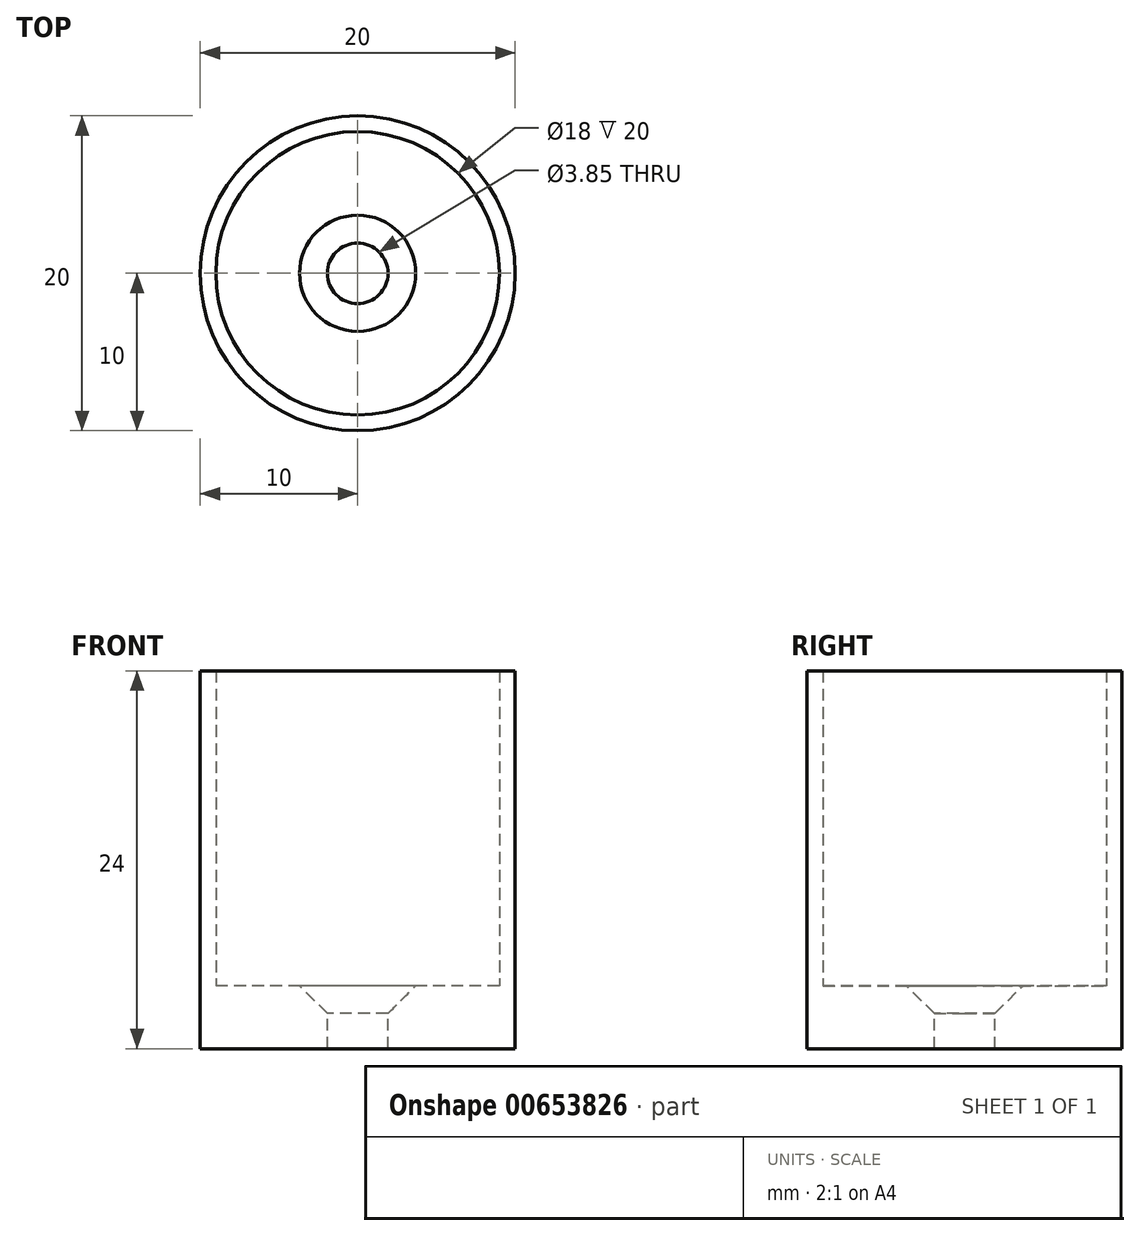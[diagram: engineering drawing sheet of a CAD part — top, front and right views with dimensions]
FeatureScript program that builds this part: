
annotation { "Feature Type Name" : "Feature", "Feature Type Description" : "" }
export const myFeature = defineFeature(function(context is Context, id is Id, definition is map)
    precondition{}
    {
        {
            var Q0;
            Q0=qCreatedBy(makeId("Top.planeOp"),FACE);
            var sketch = newSketch(context, id + "F0", { "sketchPlane" : qUnion([Q0])});
            skCircle(sketch, "E0", {"center": v(0, 0) * mm, "radius": 10 * mm});
            skCircle(sketch, "E1", {"center": v(0, 0) * mm, "radius": 9 * mm});
            skLineSegment(sketch, "E2", {"start": v(-9.77, 2.12) * mm, "end": v(9.77, 2.12) * mm});
            skSolve(sketch);
        }
        {
            var Q0;
            {var subQ0=sQuery(id+"F0.wireOp",EDGE,"E2");var subQ1=sQuery(id+"F0.wireOp",EDGE,"E0");var subQ2=makeQuery(id+"F0.imprint","INTERSECT",VERTEX,{"disambiguationData":[OD(0.0)],"derivedFrom":[subQ1,subQ0]});Q0=makeQuery(id+"F0.imprint","IMPRINT",FACE,{"disambiguationData":[TD([[makeQuery(id+"F0.imprint","IMPRINT",EDGE,{"disambiguationData":[TD([[subQ2,-1.0]])],"derivedFrom":subQ1}),1.0]])]});}
            extrude(context, id + "F1", {"entities" : qUnion([Q0]), "depth" : 20 * mm, "offsetDistance" : 25 * mm});
        }
        {
            var Q0;
            {var subQ0=sQuery(id+"F0.wireOp",EDGE,"E2");var subQ1=sQuery(id+"F0.wireOp",EDGE,"E1");var subQ2=makeQuery(id+"F0.imprint","INTERSECT",VERTEX,{"disambiguationData":[OD(0.0)],"derivedFrom":[subQ1,subQ0]});Q0=makeQuery(id+"F0.imprint","IMPRINT",FACE,{"disambiguationData":[TD([[makeQuery(id+"F0.imprint","IMPRINT",EDGE,{"disambiguationData":[TD([[subQ2,1.0]])],"derivedFrom":subQ1}),1.0]])]});}
            var Q1;
            {var subQ0=sQuery(id+"F0.wireOp",EDGE,"E2");var subQ1=sQuery(id+"F0.wireOp",EDGE,"E0");var subQ2=makeQuery(id+"F0.imprint","INTERSECT",VERTEX,{"disambiguationData":[OD(0.0)],"derivedFrom":[subQ1,subQ0]});Q1=makeQuery(id+"F0.imprint","IMPRINT",FACE,{"disambiguationData":[TD([[makeQuery(id+"F0.imprint","IMPRINT",EDGE,{"disambiguationData":[TD([[subQ2,1.0]])],"derivedFrom":subQ1}),1.0]])]});}
            var Q2;
            {var subQ0=sQuery(id+"F0.wireOp",EDGE,"E2");var subQ1=sQuery(id+"F0.wireOp",EDGE,"E0");var subQ2=makeQuery(id+"F0.imprint","INTERSECT",VERTEX,{"disambiguationData":[OD(0.0)],"derivedFrom":[subQ1,subQ0]});Q2=makeQuery(id+"F0.imprint","IMPRINT",FACE,{"disambiguationData":[TD([[makeQuery(id+"F0.imprint","IMPRINT",EDGE,{"disambiguationData":[TD([[subQ2,-1.0]])],"derivedFrom":subQ1}),1.0]])]});}
            var Q3;
            {var subQ0=sQuery(id+"F0.wireOp",EDGE,"E2");var subQ1=sQuery(id+"F0.wireOp",EDGE,"E1");var subQ2=makeQuery(id+"F0.imprint","INTERSECT",VERTEX,{"disambiguationData":[OD(0.0)],"derivedFrom":[subQ1,subQ0]});Q3=makeQuery(id+"F0.imprint","IMPRINT",FACE,{"disambiguationData":[TD([[makeQuery(id+"F0.imprint","IMPRINT",EDGE,{"disambiguationData":[TD([[subQ2,-1.0]])],"derivedFrom":subQ1}),1.0]])]});}
            extrude(context, id + "F2", {"entities" : qUnion([Q0, Q1, Q2, Q3]), "operationType" : NewBodyOperationType.ADD, "oppositeDirection" : true, "depth" : 4 * mm, "offsetDistance" : 25 * mm});
        }
        {
            var Q0;
            Q0=makeQuery(id+"F2.opExtrude","CAP_FACE",FACE,{"disambiguationData":[OSD([sQuery(id+"F0.wireOp",EDGE,"E0")])],"isStart":true});
            var sketch = newSketch(context, id + "F3", { "sketchPlane" : qUnion([Q0])});
            skCircle(sketch, "E3", {"center": v(0, 0) * mm, "radius": 1.38 * mm});
            skSolve(sketch);
        }
        {
            var Q0;
            Q0=sQuery(id+"F3.wireOp",VERTEX,"E3.center");
            var Q1;
            Q1=makeQuery(id+"F1.opExtrude","SWEPT_BODY",BODY,{"disambiguationData":[OSD([sQuery(id+"F0.wireOp",EDGE,"E0"),sQuery(id+"F0.wireOp",EDGE,"E1"),sQuery(id+"F0.wireOp",EDGE,"E2")])]});
            hole(context, id + "F4", {"style" : HoleStyle.C_SINK, "endStyle" : HoleEndStyle.THROUGH, "holeDiameter" : 3.85 * mm, "cSinkDiameter" : 7.38 * mm, "cSinkAngle" : 90 * degree, "majorDiameter" : 5 * mm, "isTappedThrough" : true, "tappedDepth" : 12 * mm, "tapClearance" : 3, "locations" : qUnion([Q0]), "scope" : qUnion([Q1])});
        }
        {
            var Q0;
            {var subQ0=sQuery(id+"F0.wireOp",EDGE,"E2");var subQ1=sQuery(id+"F0.wireOp",EDGE,"E0");var subQ2=makeQuery(id+"F0.imprint","INTERSECT",VERTEX,{"disambiguationData":[OD(0.0)],"derivedFrom":[subQ1,subQ0]});Q0=makeQuery(id+"F0.imprint","IMPRINT",FACE,{"disambiguationData":[TD([[makeQuery(id+"F0.imprint","IMPRINT",EDGE,{"disambiguationData":[TD([[subQ2,1.0]])],"derivedFrom":subQ1}),1.0]])]});}
            extrude(context, id + "F5", {"entities" : qUnion([Q0]), "operationType" : NewBodyOperationType.ADD, "depth" : 20 * mm, "offsetDistance" : 25 * mm});
        }
    });
